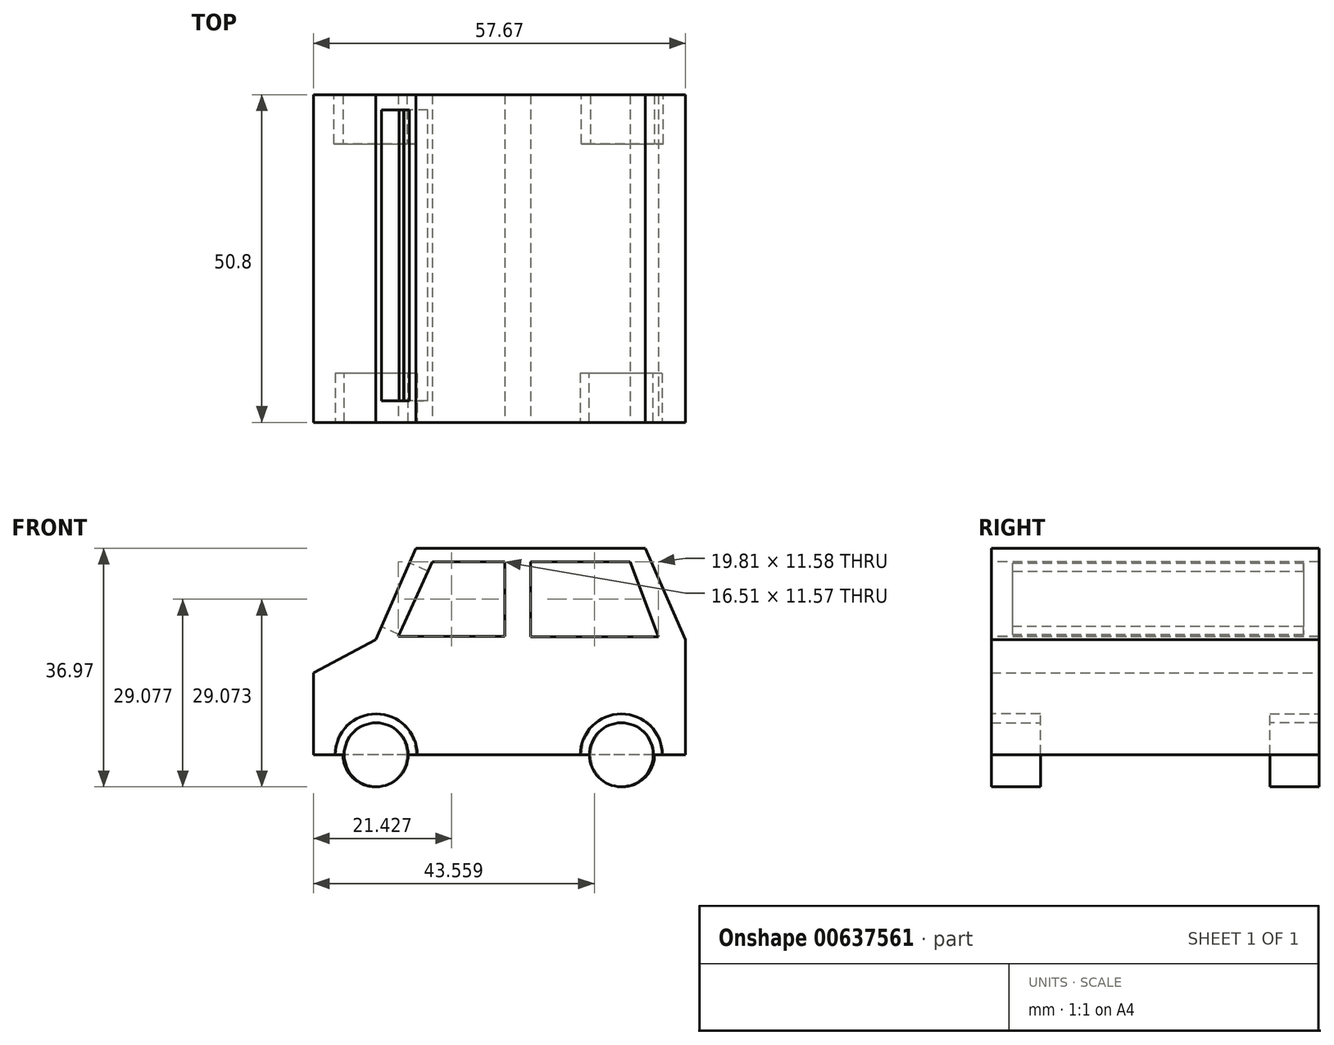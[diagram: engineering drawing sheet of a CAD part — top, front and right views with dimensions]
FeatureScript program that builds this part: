
annotation { "Feature Type Name" : "Feature", "Feature Type Description" : "" }
export const myFeature = defineFeature(function(context is Context, id is Id, definition is map)
    precondition{}
    {
        {
            var Q0;
            Q0=qCreatedBy(makeId("Front.planeOp"),FACE);
            var sketch = newSketch(context, id + "F0", { "sketchPlane" : qUnion([Q0])});
            skLineSegment(sketch, "E0", {"start": v(-75.71, 32.56) * mm, "end": v(-75.71, 45.26) * mm});
            skLineSegment(sketch, "E1", {"start": v(-75.71, 45.26) * mm, "end": v(-66.07, 50.38) * mm});
            skLineSegment(sketch, "E2", {"start": v(-66.07, 50.38) * mm, "end": v(-59.84, 64.57) * mm});
            skLineSegment(sketch, "E3", {"start": v(-59.84, 64.57) * mm, "end": v(-24.28, 64.57) * mm});
            skLineSegment(sketch, "E4", {"start": v(-24.28, 64.57) * mm, "end": v(-18.04, 50.38) * mm});
            skLineSegment(sketch, "E5", {"start": v(-18.04, 50.38) * mm, "end": v(-18.04, 34.47) * mm});
            skLineSegment(sketch, "E6", {"start": v(-18.04, 34.47) * mm, "end": v(-18.04, 32.56) * mm});
            skLineSegment(sketch, "E7", {"start": v(-18.04, 32.56) * mm, "end": v(-75.71, 32.56) * mm});
            skSolve(sketch);
        }
        {
            var Q0;
            Q0=makeQuery(id+"F0.imprint","IMPRINT",FACE,{"disambiguationData":[TD([[makeQuery(id+"F0.imprint","IMPRINT",EDGE,{"derivedFrom":sQuery(id+"F0.wireOp",EDGE,"E0")}),-1.0]])]});
            extrude(context, id + "F1", {"entities" : qUnion([Q0]), "depth" : 50.8 * mm, "offsetDistance" : 25.4 * mm});
        }
        {
            var Q0;
            Q0=makeQuery(id+"F1.opExtrude","CAP_FACE",FACE,{"disambiguationData":[OSD([sQuery(id+"F0.wireOp",EDGE,"E0"),sQuery(id+"F0.wireOp",EDGE,"E1"),sQuery(id+"F0.wireOp",EDGE,"E2"),sQuery(id+"F0.wireOp",EDGE,"E3"),sQuery(id+"F0.wireOp",EDGE,"E4"),sQuery(id+"F0.wireOp",EDGE,"E5"),sQuery(id+"F0.wireOp",EDGE,"E6"),sQuery(id+"F0.wireOp",EDGE,"E7")])],"isStart":false});
            var sketch = newSketch(context, id + "F2", { "sketchPlane" : qUnion([Q0])});
            skCircle(sketch, "E8", {"center": v(-65.97, 32.56) * mm, "radius": 6.35 * mm});
            skCircle(sketch, "E9", {"center": v(-27.02, 32.56) * mm, "radius": 6.35 * mm});
            skLineSegment(sketch, "E10", {"start": v(-56.49, 60.46) * mm, "end": v(-61.01, 51.08) * mm});
            skLineSegment(sketch, "E11", {"start": v(-61.01, 51.08) * mm, "end": v(-43.23, 51.08) * mm});
            skLineSegment(sketch, "E12", {"start": v(-43.23, 51.08) * mm, "end": v(-43.23, 60.46) * mm});
            skLineSegment(sketch, "E13", {"start": v(-43.23, 60.46) * mm, "end": v(-56.49, 60.46) * mm});
            skLineSegment(sketch, "E14", {"start": v(-39.43, 50.38) * mm, "end": v(-24.28, 50.38) * mm});
            skLineSegment(sketch, "E15", {"start": v(-24.28, 50.38) * mm, "end": v(-26.4, 60.46) * mm});
            skLineSegment(sketch, "E16", {"start": v(-26.4, 60.46) * mm, "end": v(-37.9, 60.46) * mm});
            skLineSegment(sketch, "E17", {"start": v(-39.43, 60.46) * mm, "end": v(-39.43, 50.38) * mm});
            skLineSegment(sketch, "E18", {"start": v(-39.43, 60.46) * mm, "end": v(-32.15, 60.46) * mm});
            skSolve(sketch);
        }
        {
            var Q0;
            {var subQ0=sQuery(id+"F2.wireOp",EDGE,"E8");var subQ1=makeQuery(id+"F1.opExtrude","CAP_EDGE",EDGE,{"disambiguationData":[OSD([sQuery(id+"F0.wireOp",EDGE,"E7")])],"isStart":false});var subQ2=makeQuery(id+"F2.imprint","INTERSECT",VERTEX,{"disambiguationData":[OD(0.0)],"derivedFrom":[subQ1,subQ0]});Q0=makeQuery(id+"F2.imprint","IMPRINT",FACE,{"disambiguationData":[TD([[makeQuery(id+"F2.imprint","IMPRINT",EDGE,{"disambiguationData":[TD([[subQ2,1.0]])],"derivedFrom":subQ0}),1.0]])]});}
            extrude(context, id + "F3", {"entities" : qUnion([Q0]), "operationType" : NewBodyOperationType.REMOVE, "oppositeDirection" : true, "depth" : 7.62 * mm, "offsetDistance" : 25.4 * mm});
        }
        {
            var Q0;
            Q0=makeQuery(id+"F3.boolean.opBoolean","COPY",FACE,{"derivedFrom":makeQuery(id+"F3.opExtrude","CAP_FACE",FACE,{"disambiguationData":[OSD([sQuery(id+"F0.wireOp",EDGE,"E7"),sQuery(id+"F2.wireOp",EDGE,"E8")])],"isStart":false})});
            var sketch = newSketch(context, id + "F4", { "sketchPlane" : qUnion([Q0])});
            skCircle(sketch, "E19", {"center": v(-65.97, 32.56) * mm, "radius": 4.95 * mm});
            skSolve(sketch);
        }
        {
            var Q0;
            {var subQ0=sQuery(id+"F4.wireOp",EDGE,"E19");var subQ1=makeQuery(id+"F3.boolean.opBoolean","COPY",EDGE,{"derivedFrom":makeQuery(id+"F3.opExtrude","CAP_EDGE",EDGE,{"disambiguationData":[OSD([sQuery(id+"F0.wireOp",EDGE,"E7")])],"isStart":false})});var subQ2=makeQuery(id+"F4.imprint","INTERSECT",VERTEX,{"disambiguationData":[OD(0.0)],"derivedFrom":[subQ1,subQ0]});Q0=makeQuery(id+"F4.imprint","IMPRINT",FACE,{"disambiguationData":[TD([[makeQuery(id+"F4.imprint","IMPRINT",EDGE,{"disambiguationData":[TD([[subQ2,-1.0]])],"derivedFrom":subQ0}),1.0]])]});}
            var Q1;
            {var subQ0=sQuery(id+"F4.wireOp",EDGE,"E19");var subQ1=makeQuery(id+"F3.boolean.opBoolean","COPY",EDGE,{"derivedFrom":makeQuery(id+"F3.opExtrude","CAP_EDGE",EDGE,{"disambiguationData":[OSD([sQuery(id+"F0.wireOp",EDGE,"E7")])],"isStart":false})});var subQ2=makeQuery(id+"F4.imprint","INTERSECT",VERTEX,{"disambiguationData":[OD(0.0)],"derivedFrom":[subQ1,subQ0]});Q1=makeQuery(id+"F4.imprint","IMPRINT",FACE,{"disambiguationData":[TD([[makeQuery(id+"F4.imprint","IMPRINT",EDGE,{"disambiguationData":[TD([[subQ2,1.0]])],"derivedFrom":subQ0}),1.0]])]});}
            extrude(context, id + "F5", {"entities" : qUnion([Q0, Q1]), "operationType" : NewBodyOperationType.ADD, "depth" : 7.62 * mm, "offsetDistance" : 25.4 * mm});
        }
        {
            var Q0;
            Q0=makeQuery(id+"F1.opExtrude","CAP_FACE",FACE,{"disambiguationData":[OSD([sQuery(id+"F0.wireOp",EDGE,"E0"),sQuery(id+"F0.wireOp",EDGE,"E1"),sQuery(id+"F0.wireOp",EDGE,"E2"),sQuery(id+"F0.wireOp",EDGE,"E3"),sQuery(id+"F0.wireOp",EDGE,"E4"),sQuery(id+"F0.wireOp",EDGE,"E5"),sQuery(id+"F0.wireOp",EDGE,"E6"),sQuery(id+"F0.wireOp",EDGE,"E7")])],"isStart":false});
            var sketch = newSketch(context, id + "F6", { "sketchPlane" : qUnion([Q0])});
            skCircle(sketch, "E20", {"center": v(-27.97, 32.56) * mm, "radius": 6.35 * mm});
            skSolve(sketch);
        }
        {
            var Q0;
            {var subQ0=sQuery(id+"F6.wireOp",EDGE,"E20");var subQ1=sQuery(id+"F0.wireOp",EDGE,"E7");var subQ2=sQuery(id+"F0.wireOp",EDGE,"E6");var subQ3=sQuery(id+"F0.wireOp",EDGE,"E5");var subQ4=makeQuery(id+"F3.boolean.opBoolean","SPLIT",EDGE,{"disambiguationData":[TD([makeQuery(id+"F1.opExtrude","SWEPT_FACE",FACE,{"disambiguationData":[OSD([subQ3,subQ2])]})])],"derivedFrom":makeQuery(id+"F1.opExtrude","CAP_EDGE",EDGE,{"disambiguationData":[OSD([subQ1])],"isStart":false})});var subQ5=makeQuery(id+"F6.imprint","INTERSECT",VERTEX,{"disambiguationData":[OD(0.0)],"derivedFrom":[subQ4,subQ0]});Q0=makeQuery(id+"F6.imprint","IMPRINT",FACE,{"disambiguationData":[TD([[makeQuery(id+"F6.imprint","IMPRINT",EDGE,{"disambiguationData":[TD([[subQ5,-1.0]])],"derivedFrom":subQ0}),1.0]])]});}
            extrude(context, id + "F7", {"entities" : qUnion([Q0]), "operationType" : NewBodyOperationType.REMOVE, "oppositeDirection" : true, "depth" : 7.62 * mm, "offsetDistance" : 25.4 * mm});
        }
        {
            var Q0;
            Q0=makeQuery(id+"F7.boolean.opBoolean","COPY",FACE,{"derivedFrom":makeQuery(id+"F7.opExtrude","CAP_FACE",FACE,{"disambiguationData":[OSD([sQuery(id+"F0.wireOp",EDGE,"E7"),sQuery(id+"F6.wireOp",EDGE,"E20")])],"isStart":false})});
            var sketch = newSketch(context, id + "F8", { "sketchPlane" : qUnion([Q0])});
            skCircle(sketch, "E21", {"center": v(-27.97, 32.56) * mm, "radius": 4.95 * mm});
            skSolve(sketch);
        }
        {
            var Q0;
            {var subQ0=sQuery(id+"F8.wireOp",EDGE,"E21");var subQ1=makeQuery(id+"F7.boolean.opBoolean","COPY",EDGE,{"derivedFrom":makeQuery(id+"F7.opExtrude","CAP_EDGE",EDGE,{"disambiguationData":[OSD([sQuery(id+"F0.wireOp",EDGE,"E7")])],"isStart":false})});var subQ2=makeQuery(id+"F8.imprint","INTERSECT",VERTEX,{"disambiguationData":[OD(0.0)],"derivedFrom":[subQ1,subQ0]});Q0=makeQuery(id+"F8.imprint","IMPRINT",FACE,{"disambiguationData":[TD([[makeQuery(id+"F8.imprint","IMPRINT",EDGE,{"disambiguationData":[TD([[subQ2,-1.0]])],"derivedFrom":subQ0}),1.0]])]});}
            var Q1;
            {var subQ0=sQuery(id+"F8.wireOp",EDGE,"E21");var subQ1=makeQuery(id+"F7.boolean.opBoolean","COPY",EDGE,{"derivedFrom":makeQuery(id+"F7.opExtrude","CAP_EDGE",EDGE,{"disambiguationData":[OSD([sQuery(id+"F0.wireOp",EDGE,"E7")])],"isStart":false})});var subQ2=makeQuery(id+"F8.imprint","INTERSECT",VERTEX,{"disambiguationData":[OD(0.0)],"derivedFrom":[subQ1,subQ0]});Q1=makeQuery(id+"F8.imprint","IMPRINT",FACE,{"disambiguationData":[TD([[makeQuery(id+"F8.imprint","IMPRINT",EDGE,{"disambiguationData":[TD([[subQ2,1.0]])],"derivedFrom":subQ0}),1.0]])]});}
            extrude(context, id + "F9", {"entities" : qUnion([Q0, Q1]), "operationType" : NewBodyOperationType.ADD, "depth" : 7.62 * mm, "offsetDistance" : 25.4 * mm});
        }
        {
            var Q0;
            Q0=makeQuery(id+"F1.opExtrude","CAP_FACE",FACE,{"disambiguationData":[OSD([sQuery(id+"F0.wireOp",EDGE,"E0"),sQuery(id+"F0.wireOp",EDGE,"E1"),sQuery(id+"F0.wireOp",EDGE,"E2"),sQuery(id+"F0.wireOp",EDGE,"E3"),sQuery(id+"F0.wireOp",EDGE,"E4"),sQuery(id+"F0.wireOp",EDGE,"E5"),sQuery(id+"F0.wireOp",EDGE,"E6"),sQuery(id+"F0.wireOp",EDGE,"E7")])],"isStart":false});
            var sketch = newSketch(context, id + "F10", { "sketchPlane" : qUnion([Q0])});
            skLineSegment(sketch, "E22", {"start": v(-57.31, 62.46) * mm, "end": v(-62.54, 50.89) * mm});
            skLineSegment(sketch, "E23", {"start": v(-62.54, 50.89) * mm, "end": v(-46.03, 50.89) * mm});
            skLineSegment(sketch, "E24", {"start": v(-46.03, 50.89) * mm, "end": v(-46.03, 62.46) * mm});
            skLineSegment(sketch, "E25", {"start": v(-46.03, 62.46) * mm, "end": v(-57.31, 62.46) * mm});
            skSolve(sketch);
        }
        {
            var Q0;
            Q0=makeQuery(id+"F10.imprint","IMPRINT",FACE,{"disambiguationData":[TD([[makeQuery(id+"F10.imprint","IMPRINT",EDGE,{"derivedFrom":sQuery(id+"F10.wireOp",EDGE,"E22")}),1.0]])]});
            extrude(context, id + "F11", {"entities" : qUnion([Q0]), "operationType" : NewBodyOperationType.REMOVE, "oppositeDirection" : true, "depth" : 76.2 * mm, "offsetDistance" : 25.4 * mm});
        }
        {
            var Q0;
            Q0=makeQuery(id+"F1.opExtrude","CAP_FACE",FACE,{"disambiguationData":[OSD([sQuery(id+"F0.wireOp",EDGE,"E0"),sQuery(id+"F0.wireOp",EDGE,"E1"),sQuery(id+"F0.wireOp",EDGE,"E2"),sQuery(id+"F0.wireOp",EDGE,"E3"),sQuery(id+"F0.wireOp",EDGE,"E4"),sQuery(id+"F0.wireOp",EDGE,"E5"),sQuery(id+"F0.wireOp",EDGE,"E6"),sQuery(id+"F0.wireOp",EDGE,"E7")])],"isStart":false});
            var sketch = newSketch(context, id + "F12", { "sketchPlane" : qUnion([Q0])});
            skLineSegment(sketch, "E26", {"start": v(-42.06, 62.46) * mm, "end": v(-42.06, 50.88) * mm});
            skPoint(sketch, "E26.startSnap0", {"position": v(-42.06, 64.57) * mm});
            skLineSegment(sketch, "E27", {"start": v(-42.06, 50.88) * mm, "end": v(-22.25, 50.88) * mm});
            skLineSegment(sketch, "E28", {"start": v(-22.25, 50.88) * mm, "end": v(-26.64, 62.46) * mm});
            skLineSegment(sketch, "E29", {"start": v(-26.64, 62.46) * mm, "end": v(-42.06, 62.46) * mm});
            skSolve(sketch);
        }
        {
            var Q0;
            Q0 = qSketchRegion(id + "F12", true);
            extrude(context, id + "F13", {"entities" : qUnion([Q0]), "operationType" : NewBodyOperationType.REMOVE, "oppositeDirection" : true, "depth" : 76.2 * mm, "offsetDistance" : 25.4 * mm});
        }
        {
            var Q0;
            Q0=makeQuery(id+"F1.opExtrude","SWEPT_FACE",FACE,{"disambiguationData":[OSD([sQuery(id+"F0.wireOp",EDGE,"E2")])]});
            var sketch = newSketch(context, id + "F14", { "sketchPlane" : qUnion([Q0])});
            skLineSegment(sketch, "E30", {"start": v(2.39, 32.57) * mm, "end": v(2.39, 21.78) * mm});
            skLineSegment(sketch, "E31", {"start": v(2.39, 21.78) * mm, "end": v(47.45, 21.78) * mm});
            skLineSegment(sketch, "E32", {"start": v(47.45, 21.78) * mm, "end": v(47.45, 32.57) * mm});
            skLineSegment(sketch, "E33", {"start": v(47.45, 32.57) * mm, "end": v(2.39, 32.57) * mm});
            skSolve(sketch);
        }
        {
            var Q0;
            Q0=makeQuery(id+"F14.imprint","IMPRINT",FACE,{"disambiguationData":[TD([[makeQuery(id+"F14.imprint","IMPRINT",EDGE,{"derivedFrom":sQuery(id+"F14.wireOp",EDGE,"E30")}),1.0]])]});
            extrude(context, id + "F15", {"entities" : qUnion([Q0]), "operationType" : NewBodyOperationType.REMOVE, "oppositeDirection" : true, "depth" : 3.8 * mm, "offsetDistance" : 25.4 * mm});
        }
        {
            var Q0;
            Q0=makeQuery(id+"F1.opExtrude","CAP_FACE",FACE,{"disambiguationData":[OSD([sQuery(id+"F0.wireOp",EDGE,"E0"),sQuery(id+"F0.wireOp",EDGE,"E1"),sQuery(id+"F0.wireOp",EDGE,"E2"),sQuery(id+"F0.wireOp",EDGE,"E3"),sQuery(id+"F0.wireOp",EDGE,"E4"),sQuery(id+"F0.wireOp",EDGE,"E5"),sQuery(id+"F0.wireOp",EDGE,"E6"),sQuery(id+"F0.wireOp",EDGE,"E7")])],"isStart":true});
            var sketch = newSketch(context, id + "F16", { "sketchPlane" : qUnion([Q0])});
            skCircle(sketch, "E34", {"center": v(27.78, 32.56) * mm, "radius": 6.35 * mm});
            skSolve(sketch);
        }
        {
            var Q0;
            {var subQ0=sQuery(id+"F16.wireOp",EDGE,"E34");var subQ1=makeQuery(id+"F1.opExtrude","CAP_EDGE",EDGE,{"disambiguationData":[OSD([sQuery(id+"F0.wireOp",EDGE,"E7")])],"isStart":true});var subQ2=makeQuery(id+"F16.imprint","INTERSECT",VERTEX,{"disambiguationData":[OD(0.0)],"derivedFrom":[subQ1,subQ0]});Q0=makeQuery(id+"F16.imprint","IMPRINT",FACE,{"disambiguationData":[TD([[makeQuery(id+"F16.imprint","IMPRINT",EDGE,{"disambiguationData":[TD([[subQ2,-1.0]])],"derivedFrom":subQ0}),1.0]])]});}
            extrude(context, id + "F17", {"entities" : qUnion([Q0]), "operationType" : NewBodyOperationType.REMOVE, "oppositeDirection" : true, "depth" : 7.62 * mm, "offsetDistance" : 25.4 * mm});
        }
        {
            var Q0;
            Q0=makeQuery(id+"F17.boolean.opBoolean","COPY",FACE,{"derivedFrom":makeQuery(id+"F17.opExtrude","CAP_FACE",FACE,{"disambiguationData":[OSD([sQuery(id+"F0.wireOp",EDGE,"E7"),sQuery(id+"F16.wireOp",EDGE,"E34")])],"isStart":false})});
            var sketch = newSketch(context, id + "F18", { "sketchPlane" : qUnion([Q0])});
            skCircle(sketch, "E35", {"center": v(27.78, 32.56) * mm, "radius": 4.95 * mm});
            skSolve(sketch);
        }
        {
            var Q0;
            {var subQ0=sQuery(id+"F18.wireOp",EDGE,"E35");var subQ1=makeQuery(id+"F17.boolean.opBoolean","COPY",EDGE,{"derivedFrom":makeQuery(id+"F17.opExtrude","CAP_EDGE",EDGE,{"disambiguationData":[OSD([sQuery(id+"F0.wireOp",EDGE,"E7")])],"isStart":false})});var subQ2=makeQuery(id+"F18.imprint","INTERSECT",VERTEX,{"disambiguationData":[OD(0.0)],"derivedFrom":[subQ1,subQ0]});Q0=makeQuery(id+"F18.imprint","IMPRINT",FACE,{"disambiguationData":[TD([[makeQuery(id+"F18.imprint","IMPRINT",EDGE,{"disambiguationData":[TD([[subQ2,1.0]])],"derivedFrom":subQ0}),1.0]])]});}
            var Q1;
            {var subQ0=sQuery(id+"F18.wireOp",EDGE,"E35");var subQ1=makeQuery(id+"F17.boolean.opBoolean","COPY",EDGE,{"derivedFrom":makeQuery(id+"F17.opExtrude","CAP_EDGE",EDGE,{"disambiguationData":[OSD([sQuery(id+"F0.wireOp",EDGE,"E7")])],"isStart":false})});var subQ2=makeQuery(id+"F18.imprint","INTERSECT",VERTEX,{"disambiguationData":[OD(0.0)],"derivedFrom":[subQ1,subQ0]});Q1=makeQuery(id+"F18.imprint","IMPRINT",FACE,{"disambiguationData":[TD([[makeQuery(id+"F18.imprint","IMPRINT",EDGE,{"disambiguationData":[TD([[subQ2,-1.0]])],"derivedFrom":subQ0}),1.0]])]});}
            extrude(context, id + "F19", {"entities" : qUnion([Q0, Q1]), "operationType" : NewBodyOperationType.ADD, "depth" : 7.62 * mm, "offsetDistance" : 25.4 * mm});
        }
        {
            var Q0;
            Q0=makeQuery(id+"F1.opExtrude","CAP_FACE",FACE,{"disambiguationData":[OSD([sQuery(id+"F0.wireOp",EDGE,"E0"),sQuery(id+"F0.wireOp",EDGE,"E1"),sQuery(id+"F0.wireOp",EDGE,"E2"),sQuery(id+"F0.wireOp",EDGE,"E3"),sQuery(id+"F0.wireOp",EDGE,"E4"),sQuery(id+"F0.wireOp",EDGE,"E5"),sQuery(id+"F0.wireOp",EDGE,"E6"),sQuery(id+"F0.wireOp",EDGE,"E7")])],"isStart":true});
            var sketch = newSketch(context, id + "F20", { "sketchPlane" : qUnion([Q0])});
            skCircle(sketch, "E36", {"center": v(66.17, 32.56) * mm, "radius": 6.35 * mm});
            skSolve(sketch);
        }
        {
            var Q0;
            {var subQ0=sQuery(id+"F20.wireOp",EDGE,"E36");var subQ1=sQuery(id+"F0.wireOp",EDGE,"E0");var subQ2=sQuery(id+"F0.wireOp",EDGE,"E7");var subQ3=makeQuery(id+"F17.boolean.opBoolean","SPLIT",EDGE,{"disambiguationData":[TD([makeQuery(id+"F1.opExtrude","SWEPT_FACE",FACE,{"disambiguationData":[OSD([subQ1])]})])],"derivedFrom":makeQuery(id+"F1.opExtrude","CAP_EDGE",EDGE,{"disambiguationData":[OSD([subQ2])],"isStart":true})});var subQ4=makeQuery(id+"F20.imprint","INTERSECT",VERTEX,{"disambiguationData":[OD(0.0)],"derivedFrom":[subQ3,subQ0]});Q0=makeQuery(id+"F20.imprint","IMPRINT",FACE,{"disambiguationData":[TD([[makeQuery(id+"F20.imprint","IMPRINT",EDGE,{"disambiguationData":[TD([[subQ4,-1.0]])],"derivedFrom":subQ0}),1.0]])]});}
            extrude(context, id + "F21", {"entities" : qUnion([Q0]), "operationType" : NewBodyOperationType.REMOVE, "oppositeDirection" : true, "depth" : 7.62 * mm, "offsetDistance" : 25.4 * mm});
        }
        {
            var Q0;
            Q0=makeQuery(id+"F21.boolean.opBoolean","COPY",FACE,{"derivedFrom":makeQuery(id+"F21.opExtrude","CAP_FACE",FACE,{"disambiguationData":[OSD([sQuery(id+"F0.wireOp",EDGE,"E7"),sQuery(id+"F20.wireOp",EDGE,"E36")])],"isStart":false})});
            var sketch = newSketch(context, id + "F22", { "sketchPlane" : qUnion([Q0])});
            skCircle(sketch, "E37", {"center": v(66.17, 32.56) * mm, "radius": 4.95 * mm});
            skSolve(sketch);
        }
        {
            var Q0;
            {var subQ0=sQuery(id+"F22.wireOp",EDGE,"E37");var subQ1=makeQuery(id+"F21.boolean.opBoolean","COPY",EDGE,{"derivedFrom":makeQuery(id+"F21.opExtrude","CAP_EDGE",EDGE,{"disambiguationData":[OSD([sQuery(id+"F0.wireOp",EDGE,"E7")])],"isStart":false})});var subQ2=makeQuery(id+"F22.imprint","INTERSECT",VERTEX,{"disambiguationData":[OD(0.0)],"derivedFrom":[subQ1,subQ0]});Q0=makeQuery(id+"F22.imprint","IMPRINT",FACE,{"disambiguationData":[TD([[makeQuery(id+"F22.imprint","IMPRINT",EDGE,{"disambiguationData":[TD([[subQ2,-1.0]])],"derivedFrom":subQ0}),1.0]])]});}
            var Q1;
            {var subQ0=sQuery(id+"F22.wireOp",EDGE,"E37");var subQ1=makeQuery(id+"F21.boolean.opBoolean","COPY",EDGE,{"derivedFrom":makeQuery(id+"F21.opExtrude","CAP_EDGE",EDGE,{"disambiguationData":[OSD([sQuery(id+"F0.wireOp",EDGE,"E7")])],"isStart":false})});var subQ2=makeQuery(id+"F22.imprint","INTERSECT",VERTEX,{"disambiguationData":[OD(0.0)],"derivedFrom":[subQ1,subQ0]});Q1=makeQuery(id+"F22.imprint","IMPRINT",FACE,{"disambiguationData":[TD([[makeQuery(id+"F22.imprint","IMPRINT",EDGE,{"disambiguationData":[TD([[subQ2,1.0]])],"derivedFrom":subQ0}),1.0]])]});}
            extrude(context, id + "F23", {"entities" : qUnion([Q0, Q1]), "operationType" : NewBodyOperationType.ADD, "depth" : 7.62 * mm, "offsetDistance" : 25.4 * mm});
        }
    });
